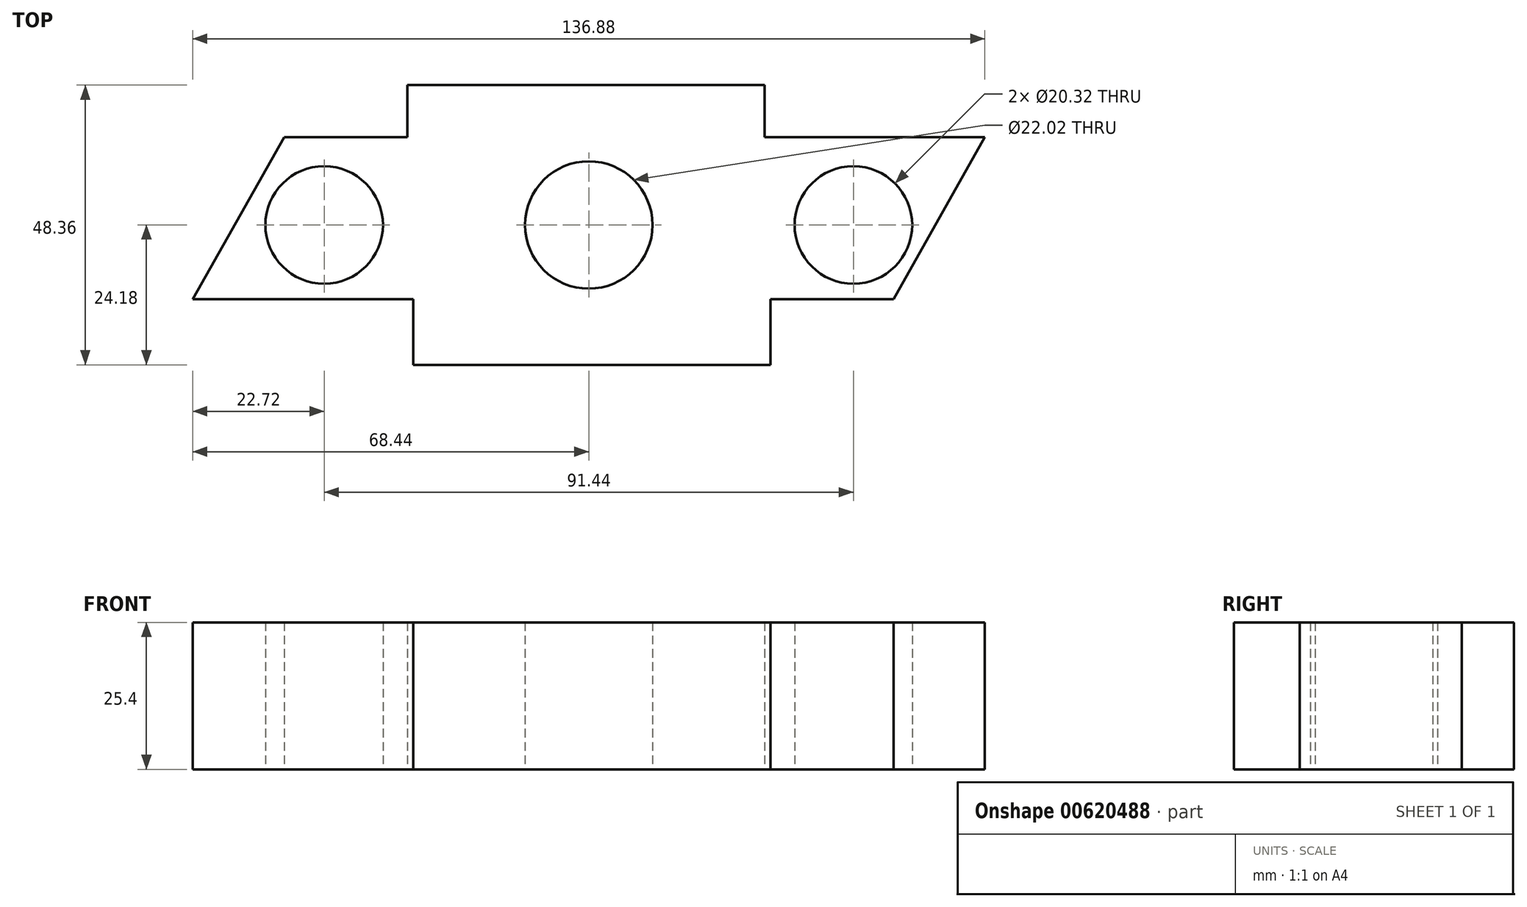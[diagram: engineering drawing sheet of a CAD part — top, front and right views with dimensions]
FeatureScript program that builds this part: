
annotation { "Feature Type Name" : "Feature", "Feature Type Description" : "" }
export const myFeature = defineFeature(function(context is Context, id is Id, definition is map)
    precondition{}
    {
        {
            var Q0;
            Q0=qCreatedBy(makeId("Top.planeOp"),FACE);
            var sketch = newSketch(context, id + "F0", { "sketchPlane" : qUnion([Q0])});
            skCircle(sketch, "E0", {"center": v(0, 0) * mm, "radius": 11.01 * mm});
            skLineSegment(sketch, "E1", {"start": v(0, 0) * mm, "end": v(-45.72, 0) * mm});
            skLineSegment(sketch, "E2", {"start": v(0, 0) * mm, "end": v(45.72, 0) * mm});
            skCircle(sketch, "E3", {"center": v(-45.72, 0) * mm, "radius": 10.16 * mm});
            skCircle(sketch, "E4", {"center": v(45.72, 0) * mm, "radius": 10.16 * mm});
            skLineSegment(sketch, "E5", {"start": v(-52.64, 15.17) * mm, "end": v(-68.44, -12.8) * mm});
            skLineSegment(sketch, "E6", {"start": v(52.64, -12.8) * mm, "end": v(68.44, 15.17) * mm});
            skLineSegment(sketch, "E7", {"start": v(-68.44, -12.8) * mm, "end": v(-30.34, -12.8) * mm});
            skLineSegment(sketch, "E8", {"start": v(-30.34, -12.8) * mm, "end": v(-30.34, -24.18) * mm});
            skLineSegment(sketch, "E9", {"start": v(-30.34, -24.18) * mm, "end": v(31.36, -24.18) * mm});
            skLineSegment(sketch, "E10", {"start": v(52.64, -12.8) * mm, "end": v(31.36, -12.8) * mm});
            skLineSegment(sketch, "E11", {"start": v(31.36, -24.18) * mm, "end": v(31.36, -12.8) * mm});
            skLineSegment(sketch, "E12", {"start": v(68.44, 15.17) * mm, "end": v(30.34, 15.17) * mm});
            skLineSegment(sketch, "E13", {"start": v(-52.64, 15.17) * mm, "end": v(-31.36, 15.17) * mm});
            skLineSegment(sketch, "E14", {"start": v(30.34, 15.17) * mm, "end": v(30.34, 24.18) * mm});
            skLineSegment(sketch, "E15", {"start": v(-31.36, 15.17) * mm, "end": v(-31.36, 24.18) * mm});
            skLineSegment(sketch, "E16", {"start": v(-31.36, 24.18) * mm, "end": v(30.34, 24.18) * mm});
            skSolve(sketch);
        }
        {
            var Q0;
            Q0 = qSketchRegion(id + "F0", true);
            extrude(context, id + "F1", {"entities" : qUnion([Q0]), "depth" : 25.4 * mm, "offsetDistance" : 25.4 * mm});
        }
    });
